# Revit family: DCS_Revit_18_CAD1-36E_Storage_593503A
name_source: partatom
category: Specialty Equipment
revit_build: Autodesk Revit 2018 (Build: 20170223_1515(x64)
units: mm (PartAtom-declared; Revit-internal decimal feet)

## family parameters
Always vertical = Yes
Cut with Voids When Loaded = Yes
OmniClass Number = 23.40.40.14.17.21
OmniClass Title = Grills
Part Type = Normal
Room Calculation Point = No
Round Connector Dimension = Use Diameter
Shared = No
Work Plane-Based = No

## types (1)
- CAD1-36E
    Chassis - Depth = 648 mm
    Chassis - Height = 816 mm
    Chassis - Width = 914 mm  [stored 2.99869 ft]
    Connector Description - Electrical = 120 V, 15A, GFI (Ground Fault Interrupter)
    Connector Description - Gas = Refer to the Grill installation guide/user guide for gas connection instructions
    Description = 36" Professional Grill Cart
    Manufacturer = Fisher & Paykel
    Material - Body = DCS - Stainless Steel
    Material - Handle = DCS - Aluminium
    Model = CAD1-36E
    Product - Depth = 678 mm
    Product - Height = 902 mm
    Product - Width = 914 mm  [stored 2.99869 ft]
    URL = www.dcsappliances.com
    Visibility - Clearance Required = Yes

note: [stored X ft] marks values corroborated as IEEE doubles in the binary element streams (Revit-internal decimal feet)

## geometry (parser evidence)
native form markers: Sweep x5
no freeform markers — native parametric forms only
